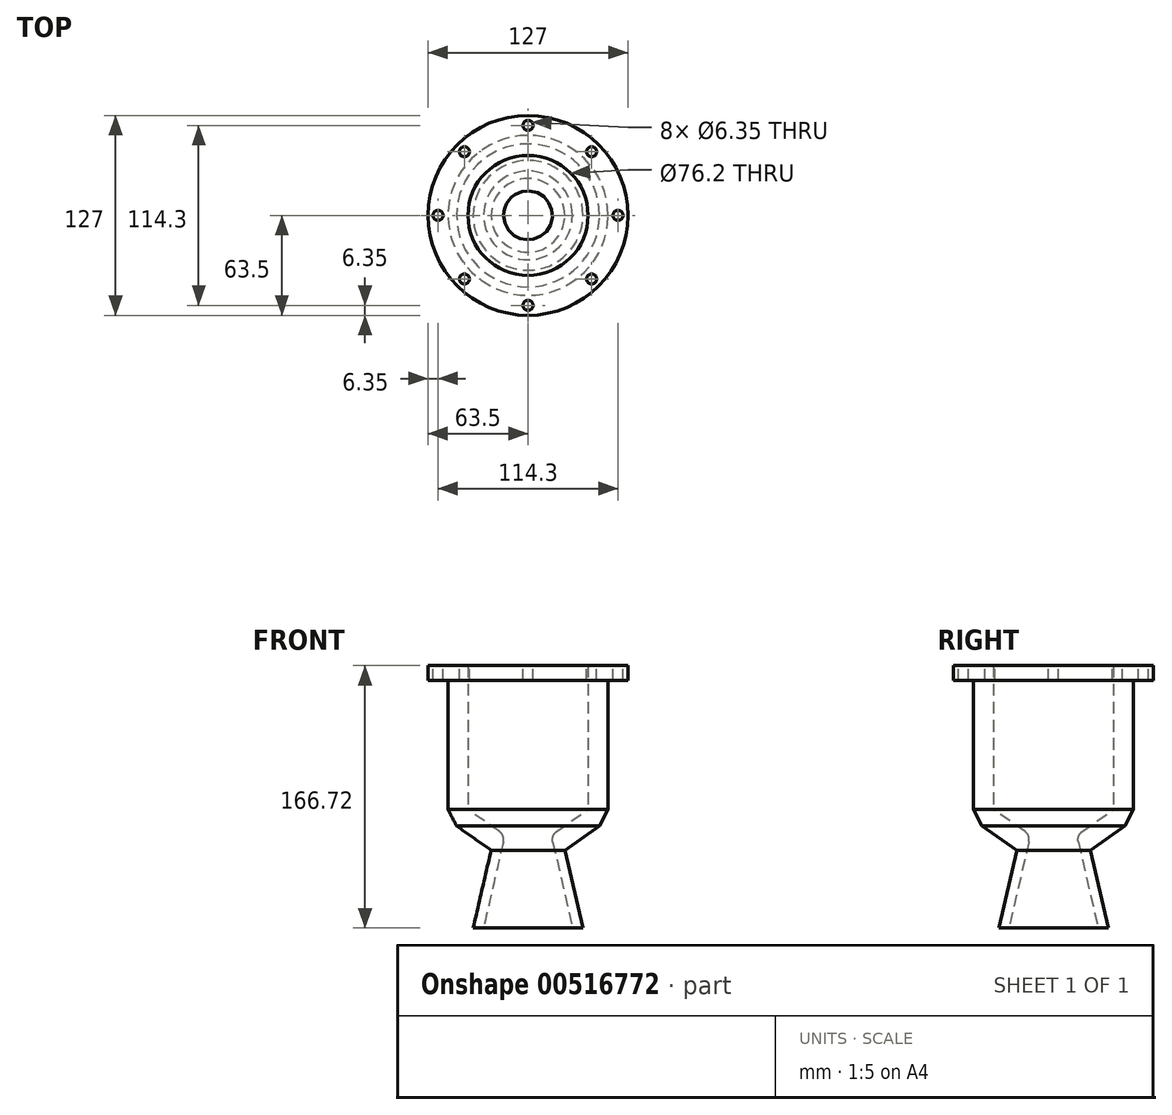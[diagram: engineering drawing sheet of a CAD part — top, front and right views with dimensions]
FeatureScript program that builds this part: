
annotation { "Feature Type Name" : "Feature", "Feature Type Description" : "" }
export const myFeature = defineFeature(function(context is Context, id is Id, definition is map)
    precondition{}
    {
        {
            var Q0;
            Q0=qCreatedBy(makeId("Front.planeOp"),FACE);
            var sketch = newSketch(context, id + "F0", { "sketchPlane" : qUnion([Q0])});
            skLineSegment(sketch, "E0", {"start": v(0, 0) * mm, "end": v(50.8, 0) * mm});
            skLineSegment(sketch, "E1.bottom", {"start": v(50.8, 0) * mm, "end": v(38.1, 0) * mm});
            skLineSegment(sketch, "E1.top", {"start": v(50.8, 91.44) * mm, "end": v(38.1, 91.44) * mm});
            skLineSegment(sketch, "E1.left", {"start": v(50.8, 0) * mm, "end": v(50.8, 91.44) * mm});
            skLineSegment(sketch, "E1.right", {"start": v(38.1, 0) * mm, "end": v(38.1, 91.44) * mm});
            skLineSegment(sketch, "E2.bottom", {"start": v(38.1, 91.44) * mm, "end": v(63.5, 91.44) * mm});
            skLineSegment(sketch, "E2.top", {"start": v(38.1, 81.91) * mm, "end": v(63.5, 81.91) * mm});
            skLineSegment(sketch, "E2.left", {"start": v(38.1, 91.44) * mm, "end": v(38.1, 81.91) * mm});
            skLineSegment(sketch, "E2.right", {"start": v(63.5, 91.44) * mm, "end": v(63.5, 81.92) * mm});
            skLineSegment(sketch, "E3", {"start": v(0, 0) * mm, "end": v(14.73, 0) * mm});
            skLineSegment(sketch, "E4", {"start": v(38.1, 0) * mm, "end": v(18.24, -13.9) * mm});
            skLineSegment(sketch, "E5", {"start": v(38.1, 0) * mm, "end": v(45.38, -10.4) * mm});
            skLineSegment(sketch, "E6", {"start": v(50.8, 0) * mm, "end": v(45.38, -10.4) * mm});
            skLineSegment(sketch, "E7", {"start": v(0, 0) * mm, "end": v(28.2, 0) * mm});
            skLineSegment(sketch, "E8", {"start": v(15.7, -20.54) * mm, "end": v(28.2, -74.67) * mm});
            skLineSegment(sketch, "E9", {"start": v(45.38, -10.4) * mm, "end": v(17.81, -29.7) * mm});
            skLineSegment(sketch, "E10", {"start": v(23.42, -25.78) * mm, "end": v(34.85, -75.28) * mm});
            skLineSegment(sketch, "E11", {"start": v(0, 0) * mm, "end": v(0, 80.76) * mm});
            skLineSegment(sketch, "E12", {"start": v(28.2, -74.67) * mm, "end": v(34.85, -75.28) * mm});
            skPoint(sketch, "E13.visualSharp", {"position": v(14.73, -16.36) * mm});
            skArc(sketch, "E13.filletArc", {"start": v(18.24, -13.9) * mm, "mid": v(15.95, -16.83) * mm, "end": v(15.7, -20.54) * mm});
            skLineSegment(sketch, "E14", {"start": v(0, 0) * mm, "end": v(0, -77.4) * mm});
            skSolve(sketch);
        }
        {
            var Q0;
            Q0 = qSketchRegion(id + "F0", true);
            var Q1;
            Q1=sQuery(id+"F0.wireOp",EDGE,"E11");
            revolve(context, id + "F1", {"entities" : qUnion([Q0]), "axis" : qUnion([Q1]), "revolveType" : RevolveType.FULL});
        }
        {
            var Q0;
            Q0=makeQuery(id+"F1.opRevolve","SWEPT_FACE",FACE,{"disambiguationData":[OSD([sQuery(id+"F0.wireOp",EDGE,"E2.bottom")])]});
            var sketch = newSketch(context, id + "F2", { "sketchPlane" : qUnion([Q0])});
            skArc(sketch, "E15", {"start": v(40.41, 40.41) * mm, "mid": v(23.33, 52.17) * mm, "end": v(3.17, 57.06) * mm});
            skCircle(sketch, "E16", {"center": v(0, 57.15) * mm, "radius": 3.18 * mm});
            skCircle(sketch, "E17.1.0", {"center": v(-40.41, 40.41) * mm, "radius": 3.18 * mm});
            skCircle(sketch, "E17.2.0", {"center": v(-57.15, 0) * mm, "radius": 3.18 * mm});
            skCircle(sketch, "E17.3.0", {"center": v(-40.41, -40.41) * mm, "radius": 3.18 * mm});
            skCircle(sketch, "E17.4.0", {"center": v(0, -57.15) * mm, "radius": 3.18 * mm});
            skCircle(sketch, "E17.5.0", {"center": v(40.41, -40.41) * mm, "radius": 3.18 * mm});
            skCircle(sketch, "E17.6.0", {"center": v(57.15, 0) * mm, "radius": 3.18 * mm});
            skCircle(sketch, "E17.7.0", {"center": v(40.41, 40.41) * mm, "radius": 3.18 * mm});
            skArc(sketch, "E18.trimOffspring", {"start": v(57.15, 0) * mm, "mid": v(53.39, 20.4) * mm, "end": v(42.6, 38.1) * mm});
            skArc(sketch, "E19.trimOffspring", {"start": v(40.41, -40.41) * mm, "mid": v(52.17, -23.33) * mm, "end": v(57.06, -3.17) * mm});
            skArc(sketch, "E20.trimOffspring", {"start": v(0, -57.15) * mm, "mid": v(20.4, -53.39) * mm, "end": v(38.1, -42.6) * mm});
            skArc(sketch, "E21.trimOffspring", {"start": v(-40.41, -40.41) * mm, "mid": v(-23.33, -52.17) * mm, "end": v(-3.17, -57.06) * mm});
            skArc(sketch, "E22.trimOffspring", {"start": v(-57.15, 0) * mm, "mid": v(-53.39, -20.4) * mm, "end": v(-42.6, -38.1) * mm});
            skArc(sketch, "E23.trimOffspring", {"start": v(-40.41, 40.41) * mm, "mid": v(-52.17, 23.33) * mm, "end": v(-57.06, 3.17) * mm});
            skArc(sketch, "E24.trimOffspring", {"start": v(0, 57.15) * mm, "mid": v(-20.4, 53.39) * mm, "end": v(-38.1, 42.6) * mm});
            skSolve(sketch);
        }
        {
            var Q0;
            {var subQ0=sQuery(id+"F2.wireOp",EDGE,"E16");var subQ1=makeQuery(id+"F2.imprint","INTERSECT",VERTEX,{"derivedFrom":[sQuery(id+"F2.wireOp",EDGE,"E15"),subQ0]});Q0=makeQuery(id+"F2.imprint","IMPRINT",FACE,{"disambiguationData":[TD([[makeQuery(id+"F2.imprint","IMPRINT",EDGE,{"disambiguationData":[TD([[subQ1,1.0]])],"derivedFrom":subQ0}),1.0]])]});}
            var Q1;
            {var subQ0=sQuery(id+"F2.wireOp",EDGE,"E17.7.0");var subQ1=makeQuery(id+"F2.imprint","INTERSECT",VERTEX,{"derivedFrom":[subQ0,sQuery(id+"F2.wireOp",EDGE,"E18.trimOffspring")]});Q1=makeQuery(id+"F2.imprint","IMPRINT",FACE,{"disambiguationData":[TD([[makeQuery(id+"F2.imprint","IMPRINT",EDGE,{"disambiguationData":[TD([[subQ1,1.0]])],"derivedFrom":subQ0}),1.0]])]});}
            var Q2;
            {var subQ0=sQuery(id+"F2.wireOp",EDGE,"E17.6.0");var subQ1=makeQuery(id+"F2.imprint","INTERSECT",VERTEX,{"derivedFrom":[subQ0,sQuery(id+"F2.wireOp",EDGE,"E19.trimOffspring")]});Q2=makeQuery(id+"F2.imprint","IMPRINT",FACE,{"disambiguationData":[TD([[makeQuery(id+"F2.imprint","IMPRINT",EDGE,{"disambiguationData":[TD([[subQ1,1.0]])],"derivedFrom":subQ0}),1.0]])]});}
            var Q3;
            {var subQ0=sQuery(id+"F2.wireOp",EDGE,"E17.5.0");var subQ1=makeQuery(id+"F2.imprint","INTERSECT",VERTEX,{"derivedFrom":[subQ0,sQuery(id+"F2.wireOp",EDGE,"E20.trimOffspring")]});Q3=makeQuery(id+"F2.imprint","IMPRINT",FACE,{"disambiguationData":[TD([[makeQuery(id+"F2.imprint","IMPRINT",EDGE,{"disambiguationData":[TD([[subQ1,1.0]])],"derivedFrom":subQ0}),1.0]])]});}
            var Q4;
            {var subQ0=sQuery(id+"F2.wireOp",EDGE,"E17.4.0");var subQ1=makeQuery(id+"F2.imprint","INTERSECT",VERTEX,{"derivedFrom":[subQ0,sQuery(id+"F2.wireOp",EDGE,"E21.trimOffspring")]});Q4=makeQuery(id+"F2.imprint","IMPRINT",FACE,{"disambiguationData":[TD([[makeQuery(id+"F2.imprint","IMPRINT",EDGE,{"disambiguationData":[TD([[subQ1,1.0]])],"derivedFrom":subQ0}),1.0]])]});}
            var Q5;
            {var subQ0=sQuery(id+"F2.wireOp",EDGE,"E17.3.0");var subQ1=makeQuery(id+"F2.imprint","INTERSECT",VERTEX,{"derivedFrom":[subQ0,sQuery(id+"F2.wireOp",EDGE,"E22.trimOffspring")]});Q5=makeQuery(id+"F2.imprint","IMPRINT",FACE,{"disambiguationData":[TD([[makeQuery(id+"F2.imprint","IMPRINT",EDGE,{"disambiguationData":[TD([[subQ1,1.0]])],"derivedFrom":subQ0}),1.0]])]});}
            var Q6;
            {var subQ0=sQuery(id+"F2.wireOp",EDGE,"E17.2.0");var subQ1=makeQuery(id+"F2.imprint","INTERSECT",VERTEX,{"derivedFrom":[subQ0,sQuery(id+"F2.wireOp",EDGE,"E23.trimOffspring")]});Q6=makeQuery(id+"F2.imprint","IMPRINT",FACE,{"disambiguationData":[TD([[makeQuery(id+"F2.imprint","IMPRINT",EDGE,{"disambiguationData":[TD([[subQ1,1.0]])],"derivedFrom":subQ0}),1.0]])]});}
            var Q7;
            {var subQ0=sQuery(id+"F2.wireOp",EDGE,"E17.1.0");var subQ1=makeQuery(id+"F2.imprint","INTERSECT",VERTEX,{"derivedFrom":[subQ0,sQuery(id+"F2.wireOp",EDGE,"E24.trimOffspring")]});Q7=makeQuery(id+"F2.imprint","IMPRINT",FACE,{"disambiguationData":[TD([[makeQuery(id+"F2.imprint","IMPRINT",EDGE,{"disambiguationData":[TD([[subQ1,1.0]])],"derivedFrom":subQ0}),1.0]])]});}
            extrude(context, id + "F3", {"entities" : qUnion([Q0, Q1, Q2, Q3, Q4, Q5, Q6, Q7]), "operationType" : NewBodyOperationType.REMOVE, "oppositeDirection" : true, "depth" : 25.4 * mm, "offsetDistance" : 25.4 * mm});
        }
    });
